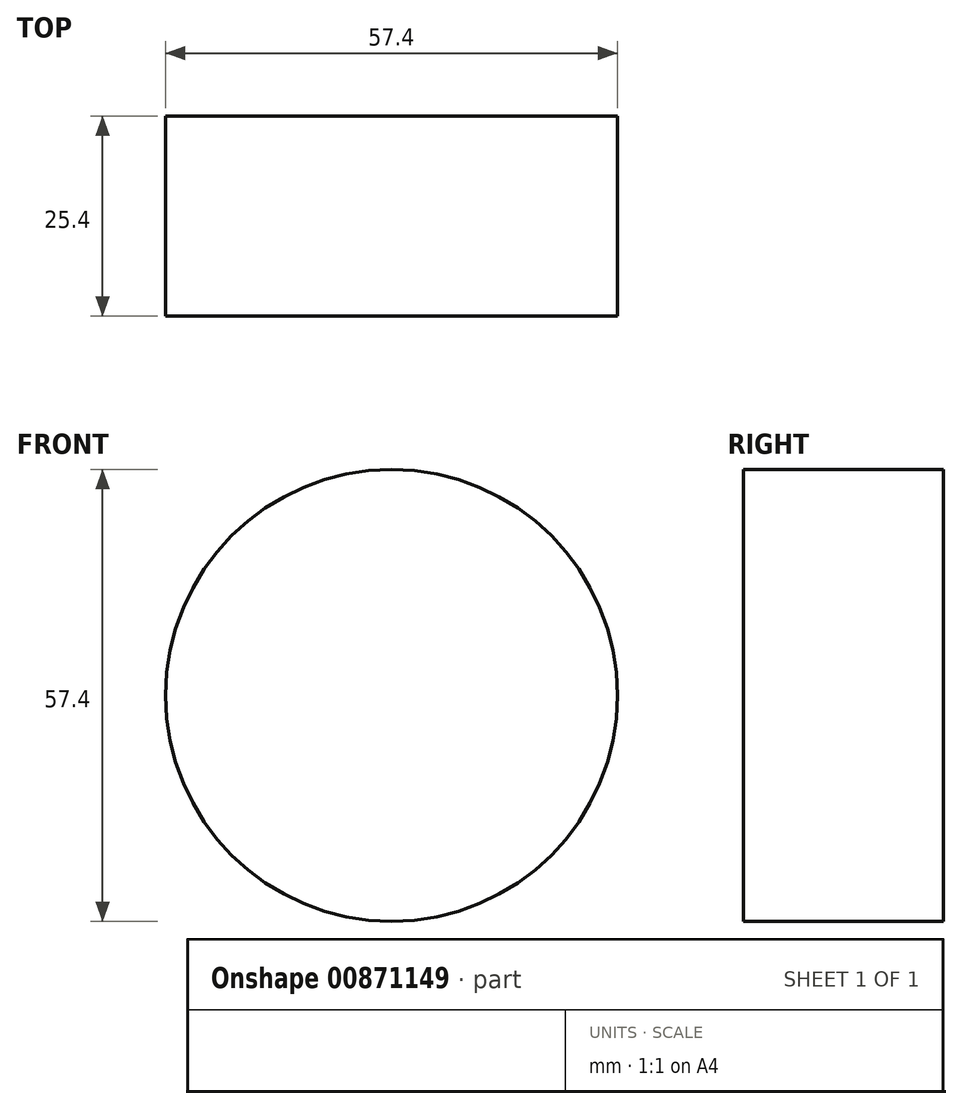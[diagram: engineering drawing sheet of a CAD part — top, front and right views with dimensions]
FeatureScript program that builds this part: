
annotation { "Feature Type Name" : "Feature", "Feature Type Description" : "" }
export const myFeature = defineFeature(function(context is Context, id is Id, definition is map)
    precondition{}
    {
        {
            var Q0;
            Q0=qCreatedBy(makeId("Front.planeOp"),FACE);
            var sketch = newSketch(context, id + "F0", { "sketchPlane" : qUnion([Q0])});
            skCircle(sketch, "E0", {"center": v(0, 0) * mm, "radius": 12.85 * mm});
            skCircle(sketch, "E1", {"center": v(0, 0) * mm, "radius": 25.6 * mm});
            skSolve(sketch);
        }
        {
            var Q0;
            Q0=makeQuery(id+"F0.imprint","IMPRINT",FACE,{"disambiguationData":[TD([[makeQuery(id+"F0.imprint","IMPRINT",EDGE,{"derivedFrom":sQuery(id+"F0.wireOp",EDGE,"E0")}),1.0]])]});
            extrude(context, id + "F1", {"entities" : qUnion([Q0]), "depth" : 18.62 * mm, "offsetDistance" : 25.4 * mm});
        }
        {
            var Q0;
            Q0=qCreatedBy(makeId("Front.planeOp"),FACE);
            var sketch = newSketch(context, id + "F2", { "sketchPlane" : qUnion([Q0])});
            skCircle(sketch, "E2", {"center": v(0, 0) * mm, "radius": 28.7 * mm});
            skSolve(sketch);
        }
        {
            var Q0;
            Q0=makeQuery(id+"F2.imprint","IMPRINT",FACE,{"disambiguationData":[TD([[makeQuery(id+"F2.imprint","IMPRINT",EDGE,{"derivedFrom":sQuery(id+"F2.wireOp",EDGE,"E2")}),1.0]])]});
            extrude(context, id + "F3", {"entities" : qUnion([Q0]), "operationType" : NewBodyOperationType.ADD, "depth" : 25.4 * mm, "offsetDistance" : 25.4 * mm});
        }
    });
